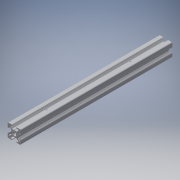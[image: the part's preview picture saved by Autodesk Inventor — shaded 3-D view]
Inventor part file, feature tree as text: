
AUTODESK INVENTOR PART (.ipt)
format: ipt  version: 2016 (Build 200138000, 138)  size: 406,528 bytes
history: native  units: in
note: dims shown in document units (in); Inventor stores cm internally (conversion verified against a paired STEP export)
features: other x3, sketch x2, extrude x1, hole x1, mirror x1
ambient origin geometry x8: Origin, YZ Plane, XZ Plane, XY Plane, X Axis, Y Axis, Z Axis, Center Point
bodies: Solid1 (feature_tree)
feature tree (8):
  other  "Blocks"
  extrude  "Extrusion1"  Depth=2.0in
  hole  "Hole1"  [1 undecoded]
  mirror  "Mirror1"
  sketch  "Sketch1"  dims[d1=0.0in d5=2.0in]
  other  "20x20"
  sketch  "Sketch3"  dims[d6=0.187in d7=0.75in d8=0.375in d9=0.25in d10=0.5635in d11=1.0in d12=0.8108in d13=1.0in d14=1.0in]
  other  "20x20:1"
note: 1 required parameter value undecoded (feature->parameter linkage not recoverable at this tier; creation-order binding heuristic only, values carry confidence <= 0.55)
